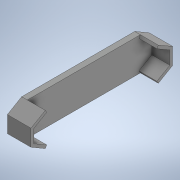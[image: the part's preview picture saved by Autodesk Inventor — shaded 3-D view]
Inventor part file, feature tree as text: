
AUTODESK INVENTOR PART (.ipt)
format: ipt  version: 2020 (Build 240168000, 168)  size: 140,800 bytes
history: native  units: in
note: dims shown in document units (in); Inventor stores cm internally (conversion verified against a paired STEP export)
features: extrude x2, sketch x2
ambient origin geometry x8: Origin, YZ Plane, XZ Plane, XY Plane, X Axis, Y Axis, Z Axis, Center Point
bodies: Solid1 (feature_tree)
feature tree (4):
  extrude  "Extrusion1"  Depth=5.9055in
  extrude  "Extrusion2"  TaperAngle=0.0deg  [1 undecoded]
  sketch  "Sketch1"  dims[d0=1.378in d1=5.9055in]
  sketch  "Sketch2"  dims[d2=0.2362in d3=0.0in d4=0.1181in d5=0.748in d6=0.0in d7=0.1181in]
note: 1 required parameter value undecoded (feature->parameter linkage not recoverable at this tier; creation-order binding heuristic only, values carry confidence <= 0.55)
